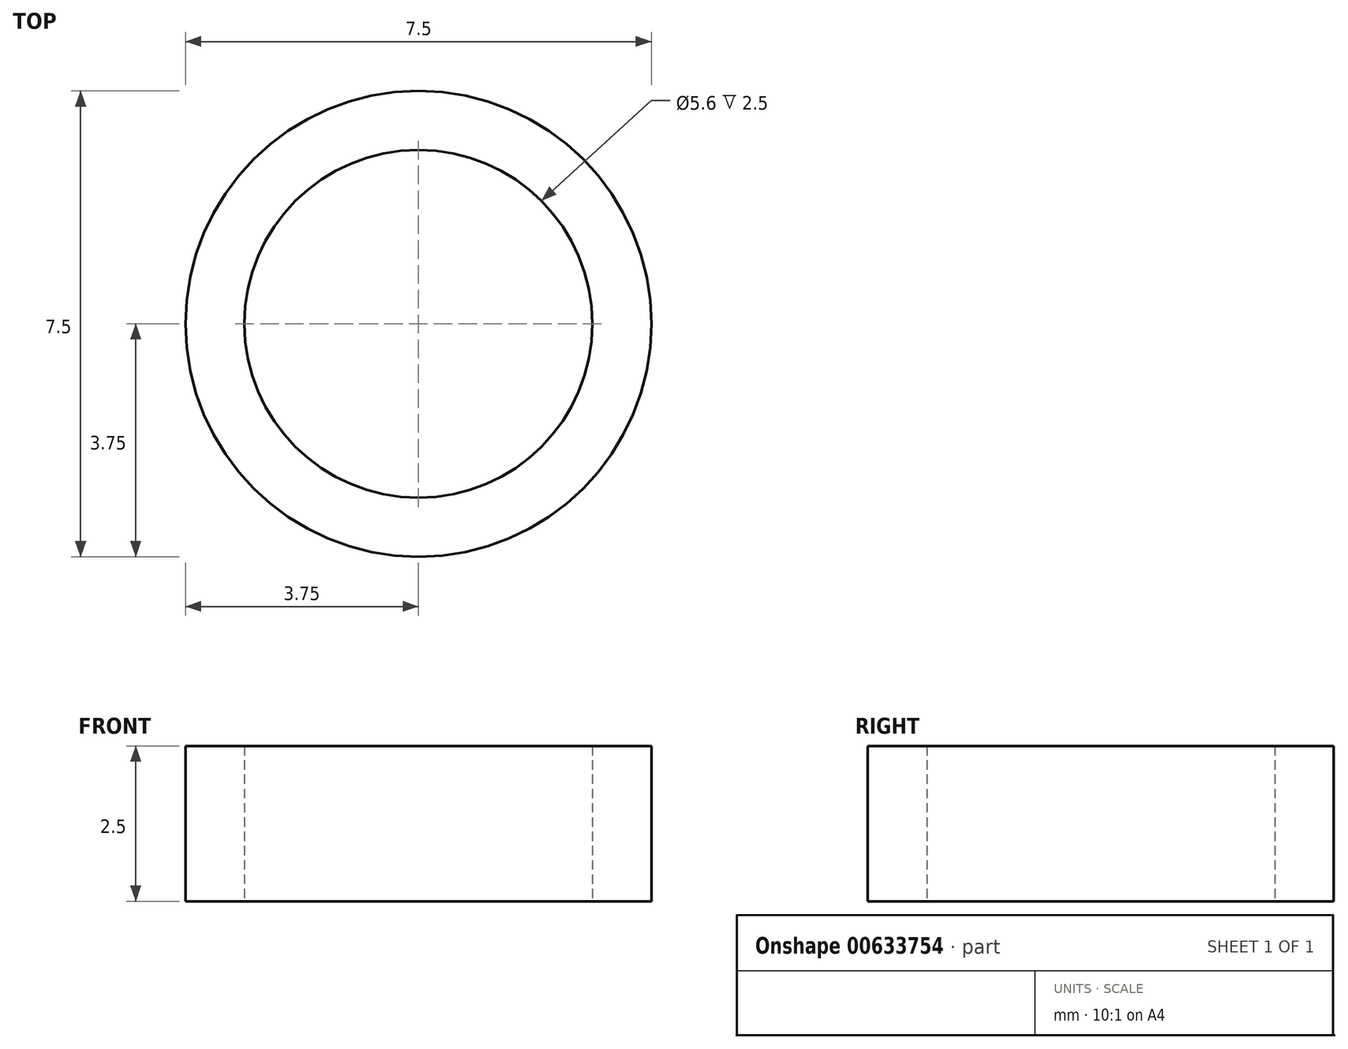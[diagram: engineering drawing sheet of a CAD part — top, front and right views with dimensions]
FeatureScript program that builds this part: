
annotation { "Feature Type Name" : "Feature", "Feature Type Description" : "" }
export const myFeature = defineFeature(function(context is Context, id is Id, definition is map)
    precondition{}
    {
        {
            var Q0;
            Q0=qCreatedBy(makeId("Top.planeOp"),FACE);
            var sketch = newSketch(context, id + "F0", { "sketchPlane" : qUnion([Q0])});
            skCircle(sketch, "E0", {"center": v(0, 0) * mm, "radius": 3.75 * mm});
            skCircle(sketch, "E1", {"center": v(0, 0) * mm, "radius": 2.8 * mm});
            skSolve(sketch);
        }
        {
            var Q0;
            Q0=makeQuery(id+"F0.imprint","IMPRINT",FACE,{"disambiguationData":[TD([[makeQuery(id+"F0.imprint","IMPRINT",EDGE,{"derivedFrom":sQuery(id+"F0.wireOp",EDGE,"E0")}),1.0]])]});
            extrude(context, id + "F1", {"entities" : qUnion([Q0]), "depth" : 2.5 * mm, "offsetDistance" : 25 * mm});
        }
    });
